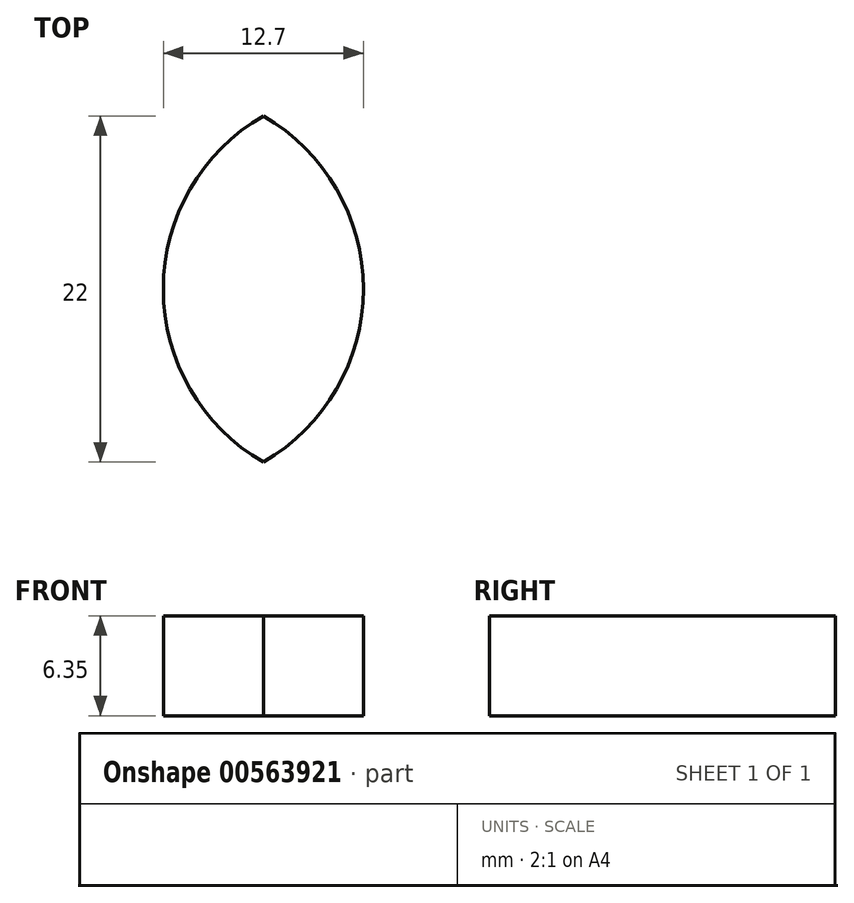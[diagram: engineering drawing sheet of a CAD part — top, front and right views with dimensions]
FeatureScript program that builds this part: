
annotation { "Feature Type Name" : "Feature", "Feature Type Description" : "" }
export const myFeature = defineFeature(function(context is Context, id is Id, definition is map)
    precondition{}
    {
        {
            var Q0;
            Q0=qCreatedBy(makeId("Top.planeOp"),FACE);
            var sketch = newSketch(context, id + "F0", { "sketchPlane" : qUnion([Q0])});
            skPoint(sketch, "E0", {"position": v(-6.35, 0) * mm});
            skPoint(sketch, "E1.MirrorP", {"position": v(6.35, 0) * mm});
            skCircle(sketch, "E2", {"center": v(-6.35, 0) * mm, "radius": 12.7 * mm});
            skCircle(sketch, "E3", {"center": v(6.35, 0) * mm, "radius": 12.7 * mm});
            skPoint(sketch, "E4", {"position": v(0, 11) * mm});
            skPoint(sketch, "E5", {"position": v(0, -11) * mm});
            skSolve(sketch);
        }
        {
            var Q0;
            {var subQ0=sQuery(id+"F0.wireOp",EDGE,"E3");var subQ1=sQuery(id+"F0.wireOp",EDGE,"E2");var subQ2=makeQuery(id+"F0.imprint","INTERSECT",VERTEX,{"disambiguationData":[OD(0.0)],"derivedFrom":[subQ1,subQ0]});Q0=makeQuery(id+"F0.imprint","IMPRINT",FACE,{"disambiguationData":[TD([[makeQuery(id+"F0.imprint","IMPRINT",EDGE,{"disambiguationData":[TD([[subQ2,-1.0]])],"derivedFrom":subQ1}),1.0]])]});}
            extrude(context, id + "F1", {"entities" : qUnion([Q0]), "depth" : 6.35 * mm, "offsetDistance" : 25.4 * mm});
        }
    });
